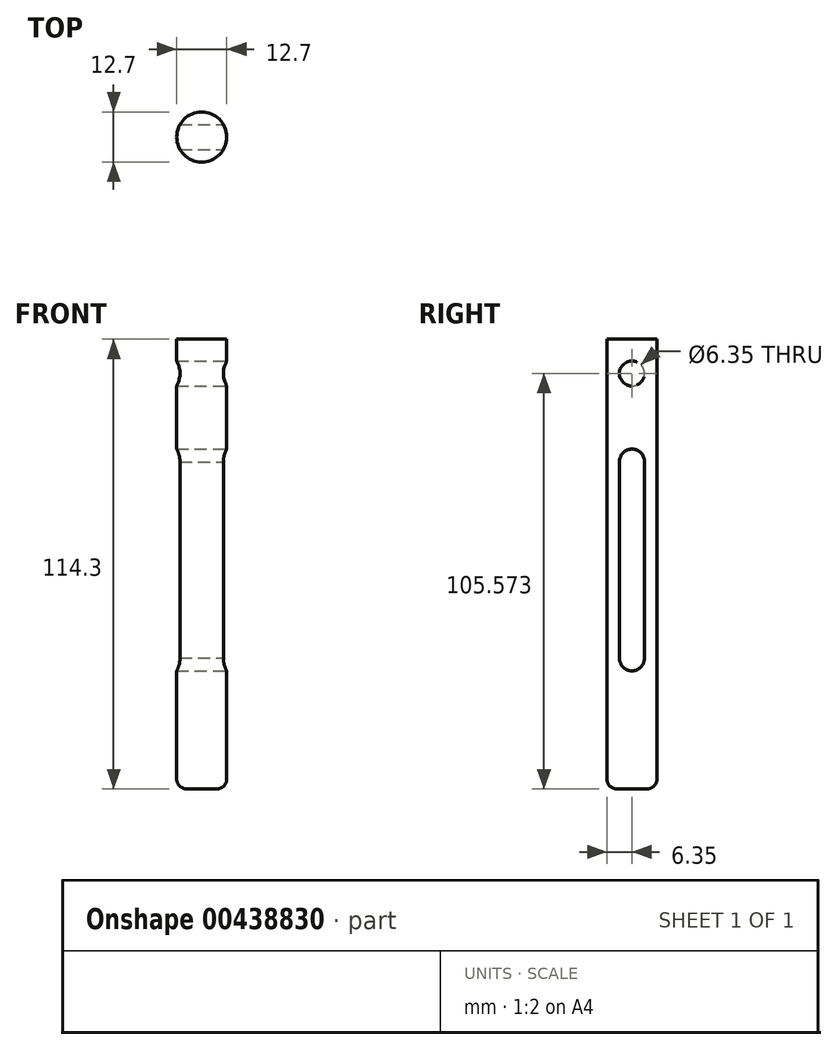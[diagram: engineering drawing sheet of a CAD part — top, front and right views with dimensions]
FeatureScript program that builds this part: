
annotation { "Feature Type Name" : "Feature", "Feature Type Description" : "" }
export const myFeature = defineFeature(function(context is Context, id is Id, definition is map)
    precondition{}
    {
        {
            var Q0;
            Q0=qCreatedBy(makeId("Top.planeOp"),FACE);
            var sketch = newSketch(context, id + "F0", { "sketchPlane" : qUnion([Q0])});
            skCircle(sketch, "E0", {"center": v(0, 0) * mm, "radius": 6.35 * mm});
            skSolve(sketch);
        }
        {
            var Q0;
            Q0 = qSketchRegion(id + "F0", true);
            extrude(context, id + "F1", {"entities" : qUnion([Q0]), "depth" : 114.3 * mm});
        }
        {
            var Q0;
            Q0=makeQuery(id+"F1.opExtrude","CAP_EDGE",EDGE,{"disambiguationData":[OSD([sQuery(id+"F0.wireOp",EDGE,"E0")])],"isStart":true});
            fillet(context, id + "F2", {"entities" : qUnion([Q0]), "radius" : 2.54 * mm, "tangentPropagation" : true, "allowEdgeOverflow" : false});
        }
        {
            var Q0;
            Q0=qCreatedBy(makeId("Right.planeOp"),FACE);
            var sketch = newSketch(context, id + "F3", { "sketchPlane" : qUnion([Q0])});
            skArc(sketch, "E1", {"start": v(3.17, 83.05) * mm, "mid": v(0, 86.36) * mm, "end": v(-3.17, 83.07) * mm});
            skArc(sketch, "E2", {"start": v(-3.17, 33.28) * mm, "mid": v(-0.06, 30) * mm, "end": v(3.17, 33.17) * mm});
            skLineSegment(sketch, "E3", {"start": v(3.17, 83.32) * mm, "end": v(3.17, 33.17) * mm});
            skLineSegment(sketch, "E4", {"start": v(-3.17, 83.3) * mm, "end": v(-3.17, 33.05) * mm});
            skSolve(sketch);
        }
        {
            var Q0;
            Q0 = qSketchRegion(id + "F3", true);
            extrude(context, id + "F4", {"entities" : qUnion([Q0]), "operationType" : NewBodyOperationType.REMOVE, "oppositeDirection" : true, "depth" : 25.4 * mm, "symmetric" : true});
        }
        {
            var Q0;
            Q0=qCreatedBy(makeId("Right.planeOp"),FACE);
            var sketch = newSketch(context, id + "F5", { "sketchPlane" : qUnion([Q0])});
            skCircle(sketch, "E5", {"center": v(0, 105.57) * mm, "radius": 3.17 * mm});
            skSolve(sketch);
        }
        {
            var Q0;
            Q0 = qSketchRegion(id + "F5", true);
            extrude(context, id + "F6", {"entities" : qUnion([Q0]), "operationType" : NewBodyOperationType.REMOVE, "oppositeDirection" : true, "depth" : 25.4 * mm, "symmetric" : true});
        }
    });
